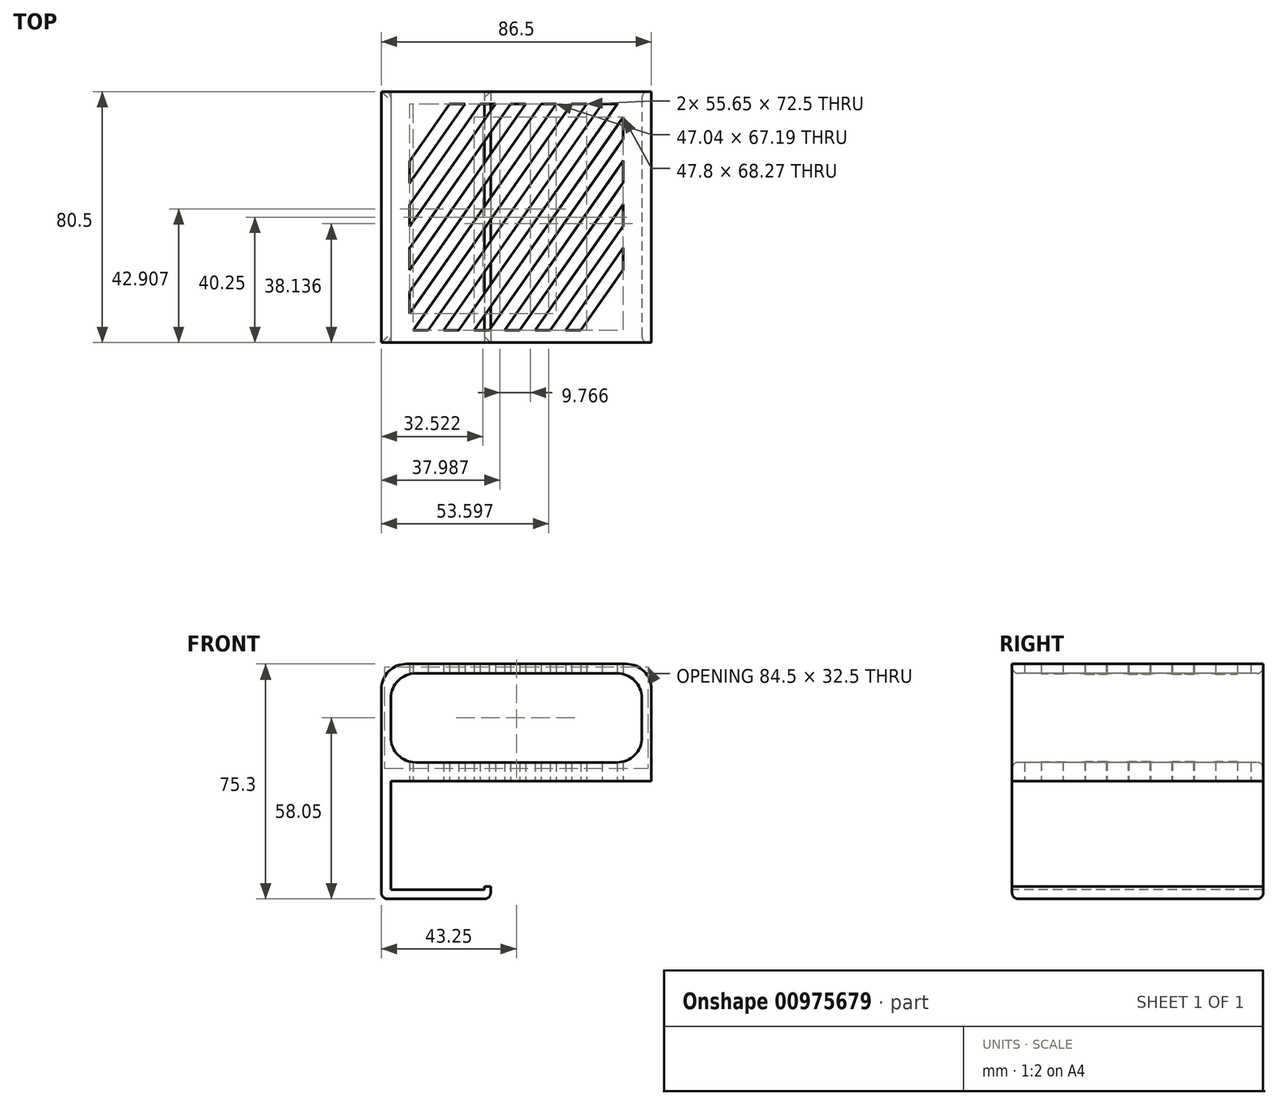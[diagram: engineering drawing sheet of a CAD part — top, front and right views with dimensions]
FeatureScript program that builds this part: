
annotation { "Feature Type Name" : "Feature", "Feature Type Description" : "" }
export const myFeature = defineFeature(function(context is Context, id is Id, definition is map)
    precondition{}
    {
        {
            var Q0;
            Q0=qCreatedBy(makeId("Front.planeOp"),FACE);
            var sketch = newSketch(context, id + "F0", { "sketchPlane" : qUnion([Q0])});
            skLineSegment(sketch, "E0.bottom", {"start": v(0, 51.9) * mm, "end": v(86.5, 51.9) * mm});
            skLineSegment(sketch, "E0.top", {"start": v(0, 17.4) * mm, "end": v(86.5, 17.4) * mm});
            skLineSegment(sketch, "E0.left", {"start": v(0, 51.9) * mm, "end": v(0, 17.4) * mm});
            skLineSegment(sketch, "E0.right", {"start": v(86.5, 51.9) * mm, "end": v(86.5, 17.4) * mm});
            skLineSegment(sketch, "E1.bottom", {"start": v(3, 48.9) * mm, "end": v(83.5, 48.9) * mm});
            skLineSegment(sketch, "E1.top", {"start": v(3, 20.4) * mm, "end": v(83.5, 20.4) * mm});
            skLineSegment(sketch, "E1.left", {"start": v(3, 48.9) * mm, "end": v(3, 20.4) * mm});
            skLineSegment(sketch, "E1.right", {"start": v(83.5, 48.9) * mm, "end": v(83.5, 20.4) * mm});
            skSolve(sketch);
        }
        {
            var Q0;
            Q0=qCreatedBy(makeId("Front.planeOp"),FACE);
            var sketch = newSketch(context, id + "F1", { "sketchPlane" : qUnion([Q0])});
            skLineSegment(sketch, "E2", {"start": v(0, 17.4) * mm, "end": v(0, -23.4) * mm});
            skPoint(sketch, "E3", {"position": v(0, 0) * mm});
            skPoint(sketch, "E4.0", {"position": v(86.5, 17.4) * mm});
            skLineSegment(sketch, "E5", {"start": v(0, 17.4) * mm, "end": v(86.5, 17.4) * mm});
            skLineSegment(sketch, "E6.0", {"start": v(3, 14.4) * mm, "end": v(86.5, 14.4) * mm});
            skLineSegment(sketch, "E7.0", {"start": v(3, 14.4) * mm, "end": v(3, -20.4) * mm});
            skLineSegment(sketch, "E8.0", {"start": v(0, -23.4) * mm, "end": v(35, -23.4) * mm});
            skLineSegment(sketch, "E9", {"start": v(3, -20.4) * mm, "end": v(35, -20.4) * mm});
            skLineSegment(sketch, "E10", {"start": v(35, -20.4) * mm, "end": v(35, -23.4) * mm});
            skLineSegment(sketch, "E11", {"start": v(86.5, 14.4) * mm, "end": v(86.5, 17.4) * mm});
            skLineSegment(sketch, "E12.bottom", {"start": v(35, -20.4) * mm, "end": v(33, -20.4) * mm});
            skLineSegment(sketch, "E12.top", {"start": v(35, -19.4) * mm, "end": v(33, -19.4) * mm});
            skLineSegment(sketch, "E12.left", {"start": v(35, -20.4) * mm, "end": v(35, -19.4) * mm});
            skLineSegment(sketch, "E12.right", {"start": v(33, -20.4) * mm, "end": v(33, -19.4) * mm});
            skSolve(sketch);
        }
        {
            var Q0;
            Q0=qCreatedBy(makeId("Top.planeOp"),FACE);
            var sketch = newSketch(context, id + "F2", { "sketchPlane" : qUnion([Q0])});
            skLineSegment(sketch, "E13", {"start": v(26.75, 76.5) * mm, "end": v(9, 51.16) * mm});
            skLineSegment(sketch, "E14.0", {"start": v(21.86, 76.5) * mm, "end": v(9, 58.13) * mm});
            skLineSegment(sketch, "E15", {"start": v(9, 51.16) * mm, "end": v(9, 58.13) * mm});
            skLineSegment(sketch, "E16", {"start": v(21.86, 76.5) * mm, "end": v(26.75, 76.5) * mm});
            skLineSegment(sketch, "E17.0", {"start": v(31.63, 76.5) * mm, "end": v(9, 44.18) * mm});
            skLineSegment(sketch, "E18.0", {"start": v(0, -5) * mm, "end": v(86.5, -5) * mm});
            skLineSegment(sketch, "E18.1", {"start": v(0, 85.5) * mm, "end": v(0, -5) * mm});
            skLineSegment(sketch, "E18.2", {"start": v(86.5, 85.5) * mm, "end": v(0, 85.5) * mm});
            skLineSegment(sketch, "E18.3", {"start": v(86.5, -5) * mm, "end": v(86.5, 85.5) * mm});
            skLineSegment(sketch, "E19.0", {"start": v(36.51, 76.5) * mm, "end": v(9, 37.2) * mm});
            skLineSegment(sketch, "E20", {"start": v(9, 37.2) * mm, "end": v(9, 44.18) * mm});
            skLineSegment(sketch, "E21", {"start": v(36.51, 76.5) * mm, "end": v(31.63, 76.5) * mm});
            skLineSegment(sketch, "E22.0", {"start": v(41.4, 76.5) * mm, "end": v(9, 30.23) * mm});
            skLineSegment(sketch, "E23.0", {"start": v(46.28, 76.5) * mm, "end": v(9, 23.26) * mm});
            skLineSegment(sketch, "E24", {"start": v(9, 23.26) * mm, "end": v(9, 30.23) * mm});
            skLineSegment(sketch, "E25", {"start": v(41.4, 76.5) * mm, "end": v(46.28, 76.5) * mm});
            skLineSegment(sketch, "E26.0", {"start": v(51.16, 76.5) * mm, "end": v(9, 16.29) * mm});
            skLineSegment(sketch, "E27.0", {"start": v(56.04, 76.5) * mm, "end": v(9, 9.31) * mm});
            skLineSegment(sketch, "E28.0", {"start": v(60.93, 76.5) * mm, "end": v(10.16, 4) * mm});
            skLineSegment(sketch, "E29.0", {"start": v(65.81, 76.5) * mm, "end": v(15.05, 4) * mm});
            skLineSegment(sketch, "E30.0", {"start": v(70.7, 76.5) * mm, "end": v(19.93, 4) * mm});
            skLineSegment(sketch, "E31.0", {"start": v(75.58, 76.5) * mm, "end": v(24.81, 4) * mm});
            skLineSegment(sketch, "E32.0", {"start": v(77.5, 72.27) * mm, "end": v(29.7, 4) * mm});
            skLineSegment(sketch, "E33.0", {"start": v(77.5, 65.3) * mm, "end": v(34.58, 4) * mm});
            skLineSegment(sketch, "E34.0", {"start": v(77.5, 58.33) * mm, "end": v(39.46, 4) * mm});
            skLineSegment(sketch, "E35.0", {"start": v(77.5, 51.35) * mm, "end": v(44.34, 4) * mm});
            skLineSegment(sketch, "E36.0", {"start": v(77.5, 44.38) * mm, "end": v(49.23, 4) * mm});
            skLineSegment(sketch, "E37.0", {"start": v(77.5, 37.4) * mm, "end": v(54.11, 4) * mm});
            skLineSegment(sketch, "E38.0", {"start": v(77.5, 30.43) * mm, "end": v(59, 4) * mm});
            skLineSegment(sketch, "E39.0", {"start": v(77.5, 23.46) * mm, "end": v(63.88, 4) * mm});
            skLineSegment(sketch, "E40", {"start": v(9, 9.31) * mm, "end": v(9, 16.29) * mm});
            skLineSegment(sketch, "E41", {"start": v(51.16, 76.5) * mm, "end": v(56.04, 76.5) * mm});
            skLineSegment(sketch, "E42", {"start": v(60.93, 76.5) * mm, "end": v(65.81, 76.5) * mm});
            skLineSegment(sketch, "E43", {"start": v(15.05, 4) * mm, "end": v(10.16, 4) * mm});
            skLineSegment(sketch, "E44", {"start": v(19.93, 4) * mm, "end": v(24.81, 4) * mm});
            skLineSegment(sketch, "E45", {"start": v(29.7, 4) * mm, "end": v(34.58, 4) * mm});
            skLineSegment(sketch, "E46", {"start": v(39.46, 4) * mm, "end": v(44.34, 4) * mm});
            skLineSegment(sketch, "E47", {"start": v(49.23, 4) * mm, "end": v(54.11, 4) * mm});
            skLineSegment(sketch, "E48", {"start": v(59, 4) * mm, "end": v(63.88, 4) * mm});
            skLineSegment(sketch, "E49", {"start": v(70.7, 76.5) * mm, "end": v(75.58, 76.5) * mm});
            skLineSegment(sketch, "E50", {"start": v(77.5, 72.27) * mm, "end": v(77.5, 65.3) * mm});
            skLineSegment(sketch, "E51", {"start": v(77.5, 51.35) * mm, "end": v(77.5, 58.33) * mm});
            skLineSegment(sketch, "E52", {"start": v(77.5, 44.38) * mm, "end": v(77.5, 37.4) * mm});
            skLineSegment(sketch, "E53", {"start": v(77.5, 30.43) * mm, "end": v(77.5, 23.46) * mm});
            skSolve(sketch);
        }
        {
            var Q0;
            Q0=makeQuery(id+"F0.imprint","IMPRINT",FACE,{"disambiguationData":[TD([[makeQuery(id+"F0.imprint","IMPRINT",EDGE,{"derivedFrom":sQuery(id+"F0.wireOp",EDGE,"E0.bottom")}),-1.0]])]});
            extrude(context, id + "F3", {"entities" : qUnion([Q0]), "oppositeDirection" : true, "depth" : 80.5 * mm, "offsetDistance" : 25 * mm});
        }
        {
            var Q0;
            {Q0=qUnion([makeQuery(id+"F1.imprint","IMPRINT",FACE,{"disambiguationData":[TD([[makeQuery(id+"F1.imprint","IMPRINT",EDGE,{"derivedFrom":sQuery(id+"F1.wireOp",EDGE,"E2")}),1.0]])]}),makeQuery(id+"F1.imprint","IMPRINT",FACE,{"disambiguationData":[TD([[makeQuery(id+"F1.imprint","IMPRINT",EDGE,{"derivedFrom":sQuery(id+"F1.wireOp",EDGE,"E12.top")}),1.0]])]})]);}
            var Q1;
            Q1=makeQuery(id+"F3.opExtrude","CAP_FACE",FACE,{"disambiguationData":[OSD([sQuery(id+"F0.wireOp",EDGE,"E0.bottom"),sQuery(id+"F0.wireOp",EDGE,"E0.top"),sQuery(id+"F0.wireOp",EDGE,"E0.left"),sQuery(id+"F0.wireOp",EDGE,"E0.right"),sQuery(id+"F0.wireOp",EDGE,"E1.bottom"),sQuery(id+"F0.wireOp",EDGE,"E1.top"),sQuery(id+"F0.wireOp",EDGE,"E1.left"),sQuery(id+"F0.wireOp",EDGE,"E1.right")])],"isStart":false});
            extrude(context, id + "F4", {"entities" : qUnion([Q0]), "operationType" : NewBodyOperationType.ADD, "endBound" : BoundingType.UP_TO_SURFACE, "oppositeDirection" : true, "depth" : 25 * mm, "endBoundEntityFace" : qUnion([Q1]), "offsetDistance" : 25 * mm});
        }
        {
            var Q0;
            Q0=makeQuery(id+"F2.imprint","IMPRINT",FACE,{"disambiguationData":[TD([[makeQuery(id+"F2.imprint","IMPRINT",EDGE,{"derivedFrom":sQuery(id+"F2.wireOp",EDGE,"E13")}),-1.0]])]});
            var Q1;
            Q1=makeQuery(id+"F2.imprint","IMPRINT",FACE,{"disambiguationData":[TD([[makeQuery(id+"F2.imprint","IMPRINT",EDGE,{"derivedFrom":sQuery(id+"F2.wireOp",EDGE,"E17.0")}),1.0]])]});
            var Q2;
            Q2=makeQuery(id+"F2.imprint","IMPRINT",FACE,{"disambiguationData":[TD([[makeQuery(id+"F2.imprint","IMPRINT",EDGE,{"derivedFrom":sQuery(id+"F2.wireOp",EDGE,"E22.0")}),1.0]])]});
            var Q3;
            Q3=makeQuery(id+"F2.imprint","IMPRINT",FACE,{"disambiguationData":[TD([[makeQuery(id+"F2.imprint","IMPRINT",EDGE,{"derivedFrom":sQuery(id+"F2.wireOp",EDGE,"E26.0")}),1.0]])]});
            var Q4;
            Q4=makeQuery(id+"F2.imprint","IMPRINT",FACE,{"disambiguationData":[TD([[makeQuery(id+"F2.imprint","IMPRINT",EDGE,{"derivedFrom":sQuery(id+"F2.wireOp",EDGE,"E28.0")}),1.0]])]});
            var Q5;
            Q5=makeQuery(id+"F2.imprint","IMPRINT",FACE,{"disambiguationData":[TD([[makeQuery(id+"F2.imprint","IMPRINT",EDGE,{"derivedFrom":sQuery(id+"F2.wireOp",EDGE,"E30.0")}),1.0]])]});
            var Q6;
            Q6=makeQuery(id+"F2.imprint","IMPRINT",FACE,{"disambiguationData":[TD([[makeQuery(id+"F2.imprint","IMPRINT",EDGE,{"derivedFrom":sQuery(id+"F2.wireOp",EDGE,"E32.0")}),1.0]])]});
            var Q7;
            Q7=makeQuery(id+"F2.imprint","IMPRINT",FACE,{"disambiguationData":[TD([[makeQuery(id+"F2.imprint","IMPRINT",EDGE,{"derivedFrom":sQuery(id+"F2.wireOp",EDGE,"E34.0")}),1.0]])]});
            var Q8;
            Q8=makeQuery(id+"F2.imprint","IMPRINT",FACE,{"disambiguationData":[TD([[makeQuery(id+"F2.imprint","IMPRINT",EDGE,{"derivedFrom":sQuery(id+"F2.wireOp",EDGE,"E36.0")}),1.0]])]});
            var Q9;
            Q9=makeQuery(id+"F2.imprint","IMPRINT",FACE,{"disambiguationData":[TD([[makeQuery(id+"F2.imprint","IMPRINT",EDGE,{"derivedFrom":sQuery(id+"F2.wireOp",EDGE,"E38.0")}),1.0]])]});
            var Q10;
            Q10=makeQuery(id+"F3.opExtrude","SWEPT_FACE",FACE,{"disambiguationData":[OSD([sQuery(id+"F0.wireOp",EDGE,"E0.bottom")])]});
            extrude(context, id + "F5", {"entities" : qUnion([Q0, Q1, Q2, Q3, Q4, Q5, Q6, Q7, Q8, Q9]), "operationType" : NewBodyOperationType.REMOVE, "endBound" : BoundingType.UP_TO_SURFACE, "depth" : 25 * mm, "endBoundEntityFace" : qUnion([Q10]), "offsetDistance" : 25 * mm});
        }
        {
            var Q0;
            Q0=makeQuery(id+"F3.opExtrude","SWEPT_EDGE",EDGE,{"disambiguationData":[OSD([sQuery(id+"F0.wireOp",EDGE,"E1.bottom"),sQuery(id+"F0.wireOp",EDGE,"E1.left")])]});
            var Q1;
            Q1=makeQuery(id+"F3.opExtrude","SWEPT_EDGE",EDGE,{"disambiguationData":[OSD([sQuery(id+"F0.wireOp",EDGE,"E1.top"),sQuery(id+"F0.wireOp",EDGE,"E1.left")])]});
            var Q2;
            Q2=makeQuery(id+"F3.opExtrude","SWEPT_EDGE",EDGE,{"disambiguationData":[OSD([sQuery(id+"F0.wireOp",EDGE,"E1.bottom"),sQuery(id+"F0.wireOp",EDGE,"E1.right")])]});
            var Q3;
            Q3=makeQuery(id+"F3.opExtrude","SWEPT_EDGE",EDGE,{"disambiguationData":[OSD([sQuery(id+"F0.wireOp",EDGE,"E1.top"),sQuery(id+"F0.wireOp",EDGE,"E1.right")])]});
            var Q4;
            Q4=makeQuery(id+"F3.opExtrude","SWEPT_EDGE",EDGE,{"disambiguationData":[OSD([sQuery(id+"F0.wireOp",EDGE,"E0.bottom"),sQuery(id+"F0.wireOp",EDGE,"E0.right")])]});
            var Q5;
            Q5=makeQuery(id+"F3.opExtrude","SWEPT_EDGE",EDGE,{"disambiguationData":[OSD([sQuery(id+"F0.wireOp",EDGE,"E0.top"),sQuery(id+"F0.wireOp",EDGE,"E0.right")])]});
            var Q6;
            Q6=makeQuery(id+"F3.opExtrude","SWEPT_EDGE",EDGE,{"disambiguationData":[OSD([sQuery(id+"F0.wireOp",EDGE,"E0.top"),sQuery(id+"F0.wireOp",EDGE,"E0.left")])]});
            var Q7;
            Q7=makeQuery(id+"F3.opExtrude","SWEPT_EDGE",EDGE,{"disambiguationData":[OSD([sQuery(id+"F0.wireOp",EDGE,"E0.bottom"),sQuery(id+"F0.wireOp",EDGE,"E0.left")])]});
            fillet(context, id + "F6", {"entities" : qUnion([Q0, Q1, Q2, Q3, Q4, Q5, Q6, Q7]), "radius" : 8 * mm, "tangentPropagation" : true, "allowEdgeOverflow" : false});
        }
        {
            var Q0;
            Q0=makeQuery(id+"F3.opExtrude","CAP_EDGE",EDGE,{"disambiguationData":[OSD([sQuery(id+"F0.wireOp",EDGE,"E1.top")])],"isStart":true});
            var Q1;
            Q1=makeQuery(id+"F3.opExtrude","CAP_EDGE",EDGE,{"disambiguationData":[OSD([sQuery(id+"F0.wireOp",EDGE,"E1.top")])],"isStart":false});
            var Q2;
            Q2=makeQuery(id+"F4.opExtrude","SWEPT_EDGE",EDGE,{"disambiguationData":[OSD([sQuery(id+"F1.wireOp",EDGE,"E8.0"),sQuery(id+"F1.wireOp",EDGE,"E10")])]});
            var Q3;
            Q3=makeQuery(id+"F4.opExtrude","CAP_EDGE",EDGE,{"disambiguationData":[OSD([sQuery(id+"F1.wireOp",EDGE,"E8.0")])],"isStart":true});
            var Q4;
            Q4=makeQuery(id+"F4.opExtrude","CAP_EDGE",EDGE,{"disambiguationData":[OSD([sQuery(id+"F1.wireOp",EDGE,"E8.0")])],"isStart":false});
            var Q5;
            Q5=makeQuery(id+"F4.opExtrude","SWEPT_EDGE",EDGE,{"disambiguationData":[OSD([sQuery(id+"F1.wireOp",EDGE,"E2"),sQuery(id+"F1.wireOp",EDGE,"E8.0")])]});
            fillet(context, id + "F7", {"entities" : qUnion([Q0, Q1, Q2, Q3, Q4, Q5]), "radius" : 2 * mm, "tangentPropagation" : true, "allowEdgeOverflow" : false});
        }
    });
